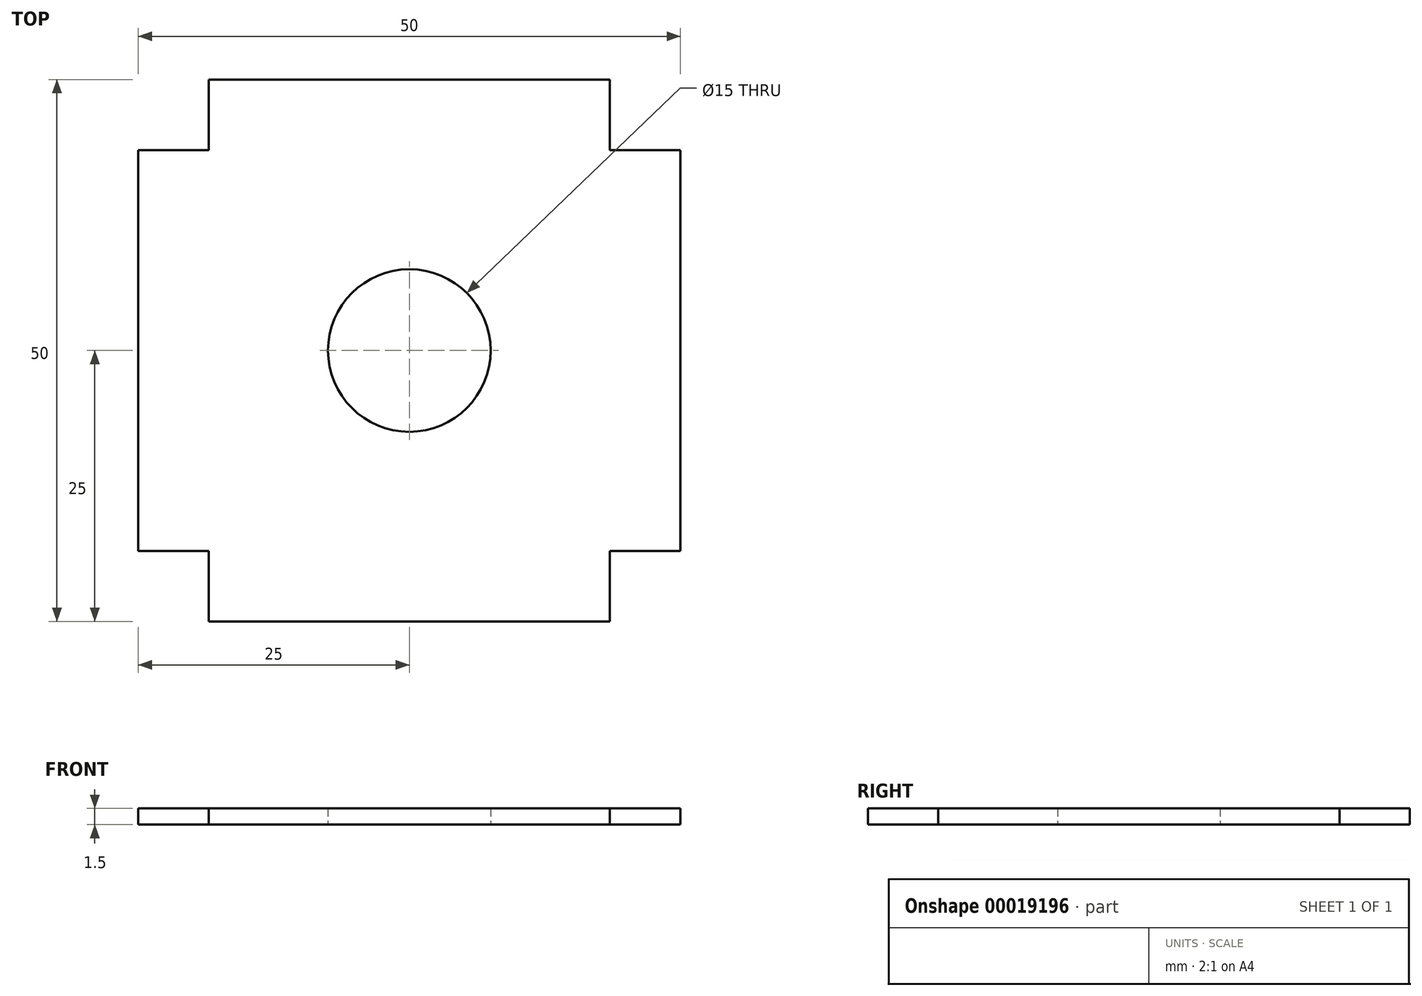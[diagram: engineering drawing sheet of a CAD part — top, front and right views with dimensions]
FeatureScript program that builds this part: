
annotation { "Feature Type Name" : "Feature", "Feature Type Description" : "" }
export const myFeature = defineFeature(function(context is Context, id is Id, definition is map)
    precondition{}
    {
        {
            var Q0;
            Q0=qCreatedBy(makeId("Top.planeOp"),FACE);
            var sketch = newSketch(context, id + "F0", { "sketchPlane" : qUnion([Q0])});
            skLineSegment(sketch, "E0.rect.bottom", {"start": v(18.5, 25) * mm, "end": v(-18.5, 25) * mm});
            skLineSegment(sketch, "E0.rect.top", {"start": v(18.5, -25) * mm, "end": v(-18.5, -25) * mm});
            skLineSegment(sketch, "E0.rect.left", {"start": v(18.5, 25) * mm, "end": v(18.5, -25) * mm});
            skLineSegment(sketch, "E0.rect.right", {"start": v(-18.5, 25) * mm, "end": v(-18.5, -25) * mm});
            skPoint(sketch, "E0.rect.middle", {"position": v(0, 0) * mm});
            skLineSegment(sketch, "E1.rect.bottom", {"start": v(25, 18.5) * mm, "end": v(-25, 18.5) * mm});
            skLineSegment(sketch, "E1.rect.top", {"start": v(25, -18.5) * mm, "end": v(-25, -18.5) * mm});
            skLineSegment(sketch, "E1.rect.left", {"start": v(25, 18.5) * mm, "end": v(25, -18.5) * mm});
            skLineSegment(sketch, "E1.rect.right", {"start": v(-25, 18.5) * mm, "end": v(-25, -18.5) * mm});
            skCircle(sketch, "E2", {"center": v(0, 0) * mm, "radius": 7.5 * mm});
            skSolve(sketch);
        }
        {
            var Q0;
            Q0 = qSketchRegion(id + "F0", true);
            extrude(context, id + "F1", {"entities" : qUnion([Q0]), "depth" : 1.5 * mm});
        }
        {
            var Q0;
            Q0 = qSketchRegion(id + "F0", true);
            extrude(context, id + "F2", {"entities" : qUnion([Q0]), "operationType" : NewBodyOperationType.ADD, "depth" : 1.2 * mm});
        }
    });
